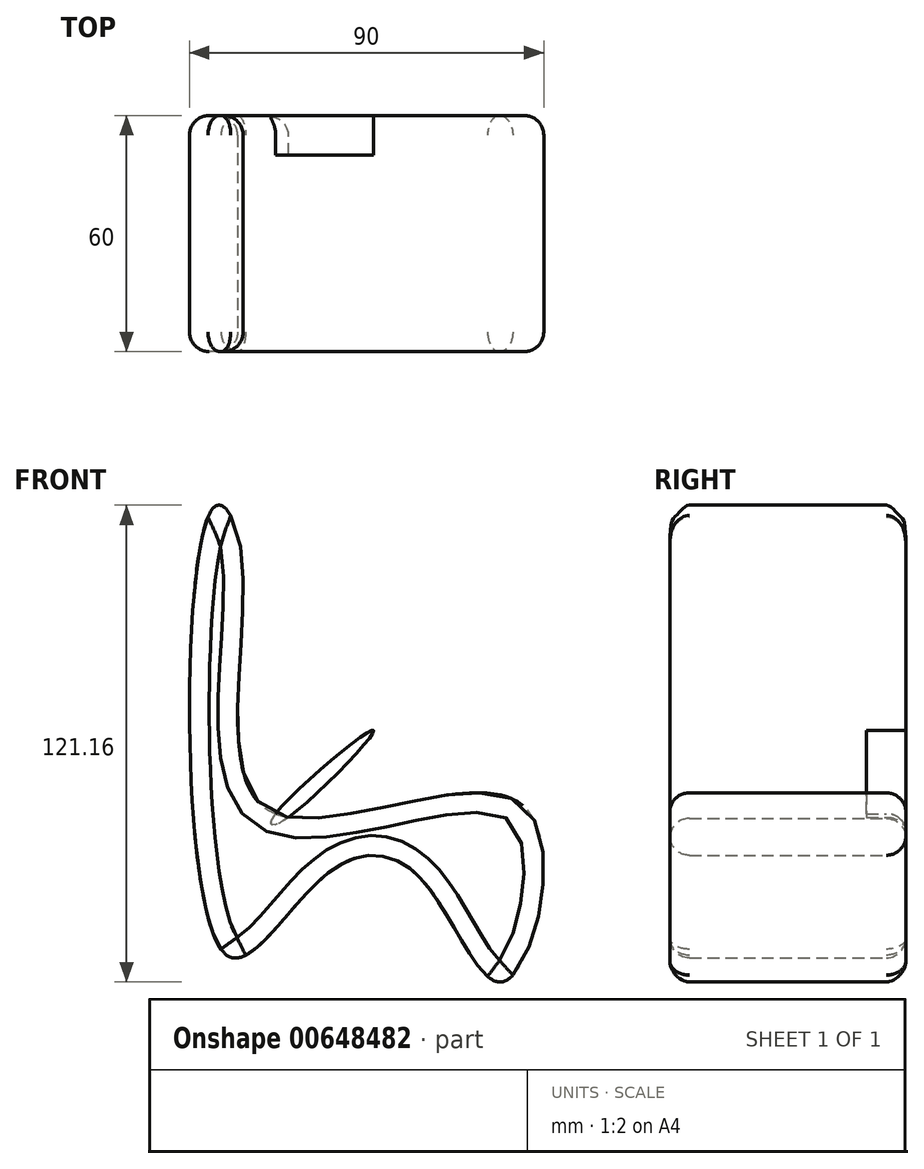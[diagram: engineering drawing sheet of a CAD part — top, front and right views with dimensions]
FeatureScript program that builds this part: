
annotation { "Feature Type Name" : "Feature", "Feature Type Description" : "" }
export const myFeature = defineFeature(function(context is Context, id is Id, definition is map)
    precondition{}
    {
        {
            var Q0;
            Q0=qCreatedBy(makeId("Front.planeOp"),FACE);
            var sketch = newSketch(context, id + "F0", { "sketchPlane" : qUnion([Q0])});
            skFitSpline(sketch, "E0", {"points": [v(-37.77, 53.63) * mm, v(-30.63, -11.6) * mm, v(34.2, -10.6) * mm, v(29.05, -54.82) * mm, v(8.03, -29.05) * mm, v(-16.16, -27.66) * mm, v(-41.94, -47.88) * mm, v(-45.3, 64.94) * mm, v(-37.77, 53.63) * mm]});
            skSolve(sketch);
        }
        {
            var Q0;
            Q0 = qSketchRegion(id + "F0", true);
            extrude(context, id + "F1", {"entities" : qUnion([Q0]), "depth" : 60 * mm, "offsetDistance" : 25 * mm});
        }
        {
            var Q0;
            Q0=makeQuery(id+"F1.opExtrude","SWEPT_FACE",FACE,{"disambiguationData":[OSD([sQuery(id+"F0.wireOp",EDGE,"E0")])]});
            fillet(context, id + "F2", {"entities" : qUnion([Q0]), "radius" : 5 * mm, "tangentPropagation" : true, "allowEdgeOverflow" : false});
        }
        {
            var Q0;
            Q0=qCreatedBy(makeId("Front.planeOp"),FACE);
            var sketch = newSketch(context, id + "F3", { "sketchPlane" : qUnion([Q0])});
            skFitSpline(sketch, "E1", {"points": [v(-30.1, -13.94) * mm, v(-4.24, 8.88) * mm, v(-28.78, -14.95) * mm, v(-30.1, -13.94) * mm]});
            skSolve(sketch);
        }
        {
            var Q0;
            Q0 = qSketchRegion(id + "F3", true);
            extrude(context, id + "F4", {"entities" : qUnion([Q0]), "operationType" : NewBodyOperationType.ADD, "depth" : 10 * mm, "offsetDistance" : 25 * mm});
        }
    });
